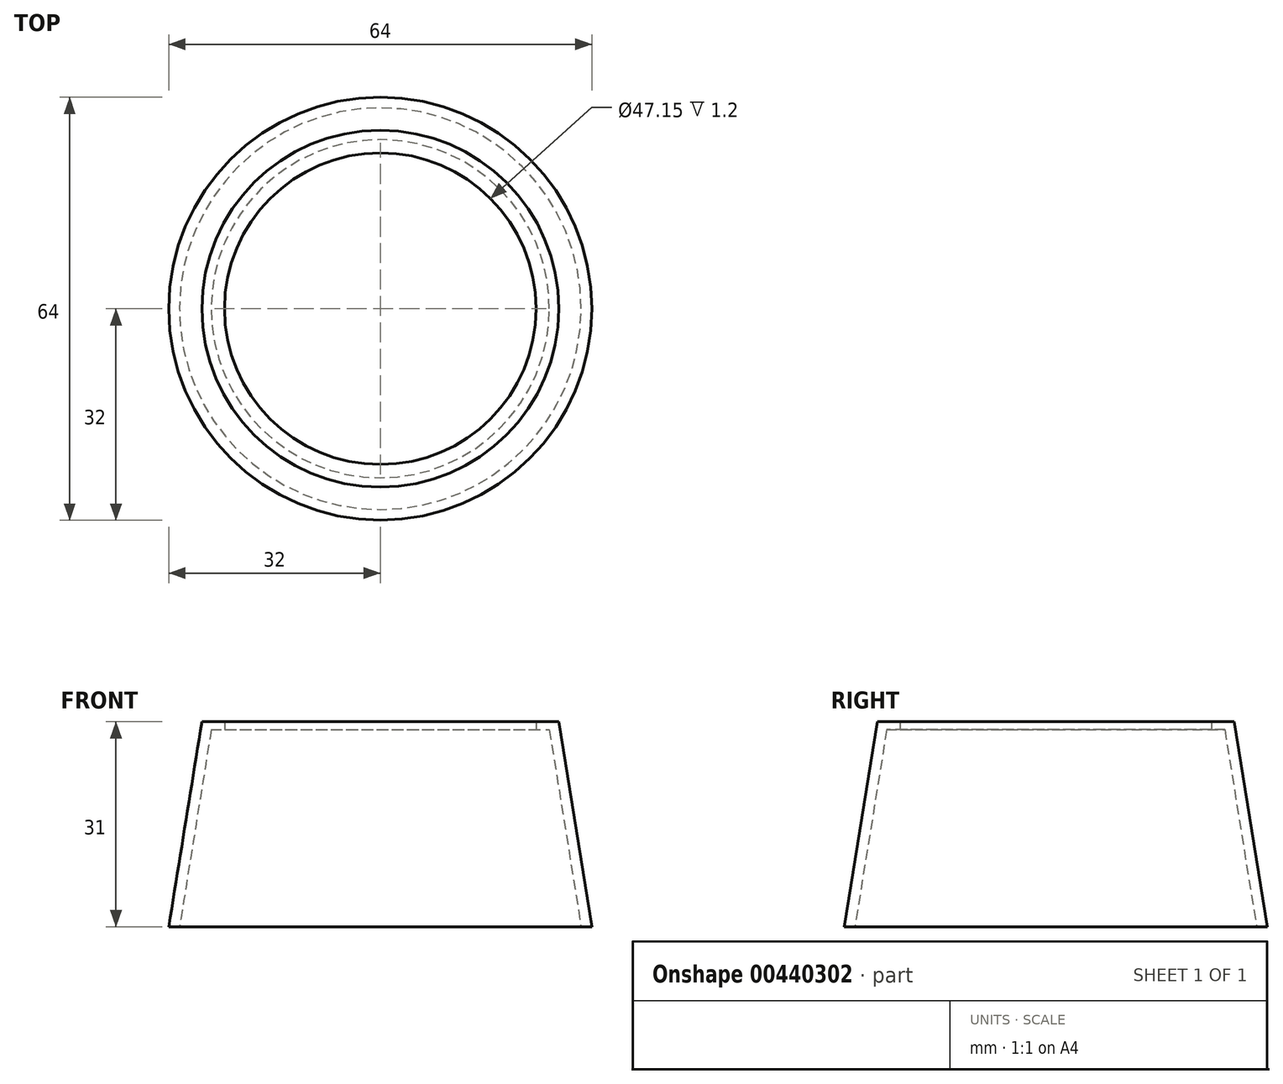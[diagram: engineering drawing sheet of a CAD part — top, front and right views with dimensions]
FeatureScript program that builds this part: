
annotation { "Feature Type Name" : "Feature", "Feature Type Description" : "" }
export const myFeature = defineFeature(function(context is Context, id is Id, definition is map)
    precondition{}
    {
        {
            var Q0;
            Q0=qCreatedBy(makeId("Front.planeOp"),FACE);
            var sketch = newSketch(context, id + "F0", { "sketchPlane" : qUnion([Q0])});
            skLineSegment(sketch, "E0", {"start": v(0, 0) * mm, "end": v(0, 40) * mm, "construction": true});
            skLineSegment(sketch, "E1", {"start": v(32, 0) * mm, "end": v(27, 31) * mm});
            skLineSegment(sketch, "E2", {"start": v(27, 31) * mm, "end": v(23.57, 31) * mm});
            skLineSegment(sketch, "E3", {"start": v(23.57, 31) * mm, "end": v(23.57, 29.8) * mm});
            skLineSegment(sketch, "E4", {"start": v(23.57, 29.8) * mm, "end": v(25.57, 29.8) * mm});
            skLineSegment(sketch, "E5", {"start": v(25.57, 29.8) * mm, "end": v(30.38, 0) * mm});
            skLineSegment(sketch, "E6", {"start": v(32, 0) * mm, "end": v(30.38, 0) * mm});
            skSolve(sketch);
        }
        {
            var Q0;
            Q0=makeQuery(id+"F0.imprint","IMPRINT",FACE,{"disambiguationData":[TD([[makeQuery(id+"F0.imprint","IMPRINT",EDGE,{"derivedFrom":sQuery(id+"F0.wireOp",EDGE,"E1")}),1.0]])]});
            var Q1;
            Q1=sQuery(id+"F0.wireOp",EDGE,"E0");
            revolve(context, id + "F1", {"entities" : qUnion([Q0]), "axis" : qUnion([Q1]), "revolveType" : RevolveType.FULL});
        }
    });
